# Revit family: Wire_w_Bracket-HunterDouglas-Echelon
name_source: partatom
category: Specialty Equipment
revit_build: Autodesk Revit Architecture 2013 (Build: 20120221_2030(x64)
units: mm (PartAtom-declared; Revit-internal decimal feet)

## types (1)
- Parametric
    04 CSI = 09 51 00
    95 CSI = 09510
    Acoustics - NRC = 0.85
    Additional Resources Note = Product details, finishes, construction details, and more can be accessed on the Product Page URL.
    Assembly Code = C3030210
    Color Finishes = http://www.hunterdouglascontract.com
    Description = Echelon Frame and Panel System
    Different Colors Available = Yes
    Fire Rating = Class A
    Flame Spread Index = 25
    GREENGUARD Certified = Yes
    GREENGUARD URL = http://assets.hunterdouglascontract.com
    High Durability = Yes
    Humidity and Sag Resistant = Yes
    Installation URL = http://www.hunterdouglascontract.com
    Light Reflectance Average = 1
    Manufacturer = Hunter Douglas Luxalon Metal Ceilings
    Material = Aluminum
    Model = Echelon
    Mold Resistant = Yes
    Panel Length Availability = 24", 30", 48"
    Panel Width Availability = 6” in increments of 6" up to 72"  and up to 96" (for 24" W Only)
    Perforations = http://www.hunterdouglascontract.com
    Product Line = Echelon System
    Product Page URL = http://www.hunterdouglascontract.com
    Recyclable = Yes
    Recycled Content Percentage = 70%
    Smoke Developed Index = 50
    Subcategory = Echelon
    Submittal URL = http://www.hunterdouglascontract.com
    Technical Information = http://assets.hunterdouglascontract.com
    URL = http://www.hunterdouglasceilings.com
    VOC Data URL = http://assets.hunterdouglascontract.com
    Warranty URL = http://www.hunterdouglascontract.com
    Wire Hanger = Metal - Aluminum Frame - HunterDouglas - Painted White
    ecoScorecard Product Page = http://hunterdouglascontract.ecoscorecard.com
    ecoScorecard_data = http://products.ecoscorecard.com

## geometry (parser evidence)
native form markers: Sweep x4
no freeform markers — native parametric forms only
